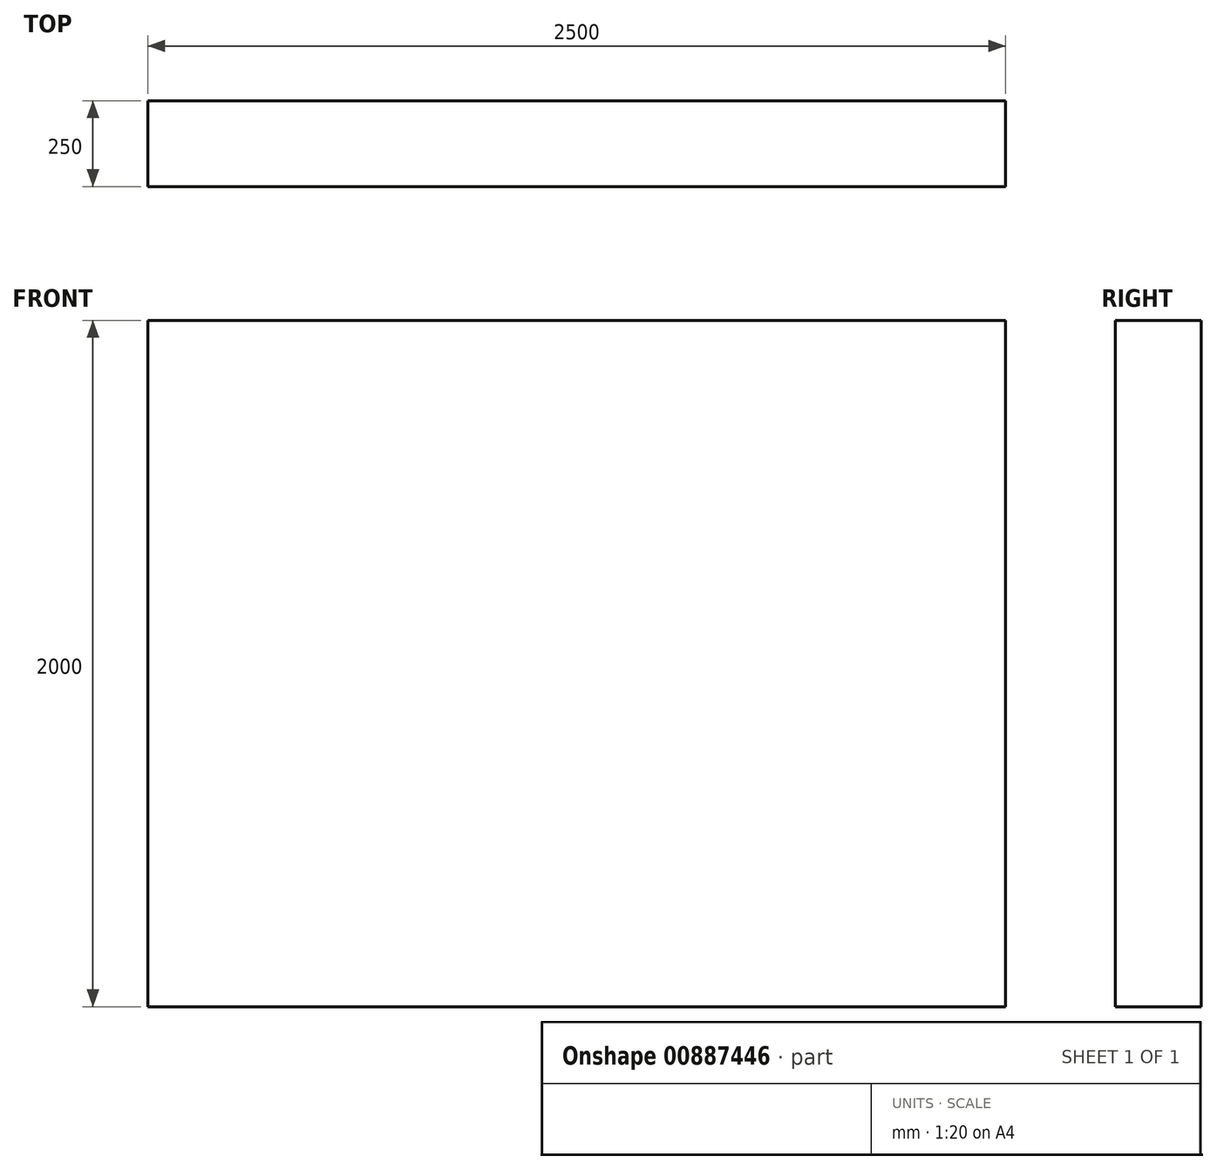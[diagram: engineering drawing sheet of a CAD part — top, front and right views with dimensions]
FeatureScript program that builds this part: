
annotation { "Feature Type Name" : "Feature", "Feature Type Description" : "" }
export const myFeature = defineFeature(function(context is Context, id is Id, definition is map)
    precondition{}
    {
        {
            var Q0;
            Q0=qCreatedBy(makeId("Front.planeOp"),FACE);
            var sketch = newSketch(context, id + "F0", { "sketchPlane" : qUnion([Q0])});
            skLineSegment(sketch, "E0.bottom", {"start": v(1250, -1000) * mm, "end": v(-1250, -1000) * mm});
            skLineSegment(sketch, "E0.top", {"start": v(1250, 1000) * mm, "end": v(-1250, 1000) * mm});
            skLineSegment(sketch, "E0.left", {"start": v(1250, -1000) * mm, "end": v(1250, 1000) * mm});
            skLineSegment(sketch, "E0.right", {"start": v(-1250, -1000) * mm, "end": v(-1250, 1000) * mm});
            skPoint(sketch, "E0.middle", {"position": v(0, 0) * mm});
            skSolve(sketch);
        }
        {
            var Q0;
            Q0=makeQuery(id+"F0.imprint","IMPRINT",FACE,{"disambiguationData":[TD([[makeQuery(id+"F0.imprint","IMPRINT",EDGE,{"derivedFrom":sQuery(id+"F0.wireOp",EDGE,"E0.bottom")}),-1.0]])]});
            extrude(context, id + "F1", {"entities" : qUnion([Q0]), "depth" : 250 * mm, "offsetDistance" : 25 * mm});
        }
    });
